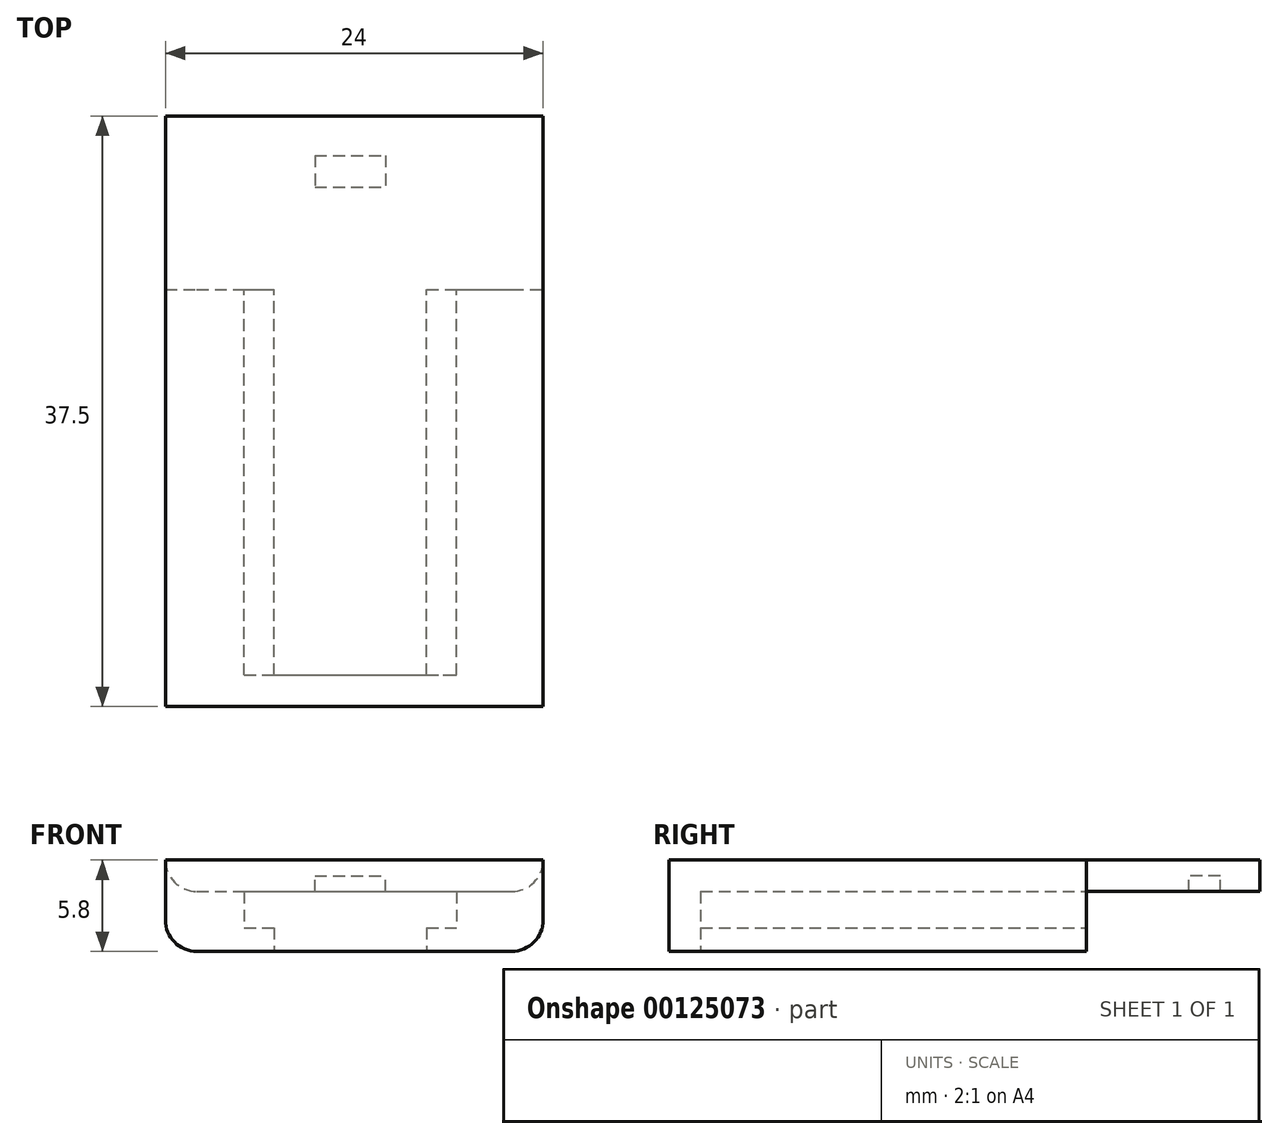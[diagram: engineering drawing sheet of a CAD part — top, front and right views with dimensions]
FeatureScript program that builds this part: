
annotation { "Feature Type Name" : "Feature", "Feature Type Description" : "" }
export const myFeature = defineFeature(function(context is Context, id is Id, definition is map)
    precondition{}
    {
        {
            var Q0;
            Q0=qCreatedBy(makeId("Front.planeOp"),FACE);
            var sketch = newSketch(context, id + "F0", { "sketchPlane" : qUnion([Q0])});
            skLineSegment(sketch, "E0.bottom", {"start": v(-6.75, 4.5) * mm, "end": v(-3.2, 4.5) * mm});
            skLineSegment(sketch, "E0.top", {"start": v(-6.75, 2.2) * mm, "end": v(-3.45, 2.2) * mm});
            skLineSegment(sketch, "E0.left", {"start": v(-6.75, 4.5) * mm, "end": v(-6.75, 2.2) * mm});
            skLineSegment(sketch, "E0.right", {"start": v(6.75, 4.5) * mm, "end": v(6.75, 2.2) * mm});
            skPoint(sketch, "E0.middle", {"position": v(0, 3.35) * mm});
            skLineSegment(sketch, "E1", {"start": v(4.85, 4.5) * mm, "end": v(4.85, 0) * mm});
            skLineSegment(sketch, "E2", {"start": v(-7.46, 0) * mm, "end": v(7.46, 0) * mm});
            skLineSegment(sketch, "E3.MirrorCS", {"start": v(-4.85, 4.5) * mm, "end": v(-4.85, 0) * mm});
            skLineSegment(sketch, "E4.trimOffspring", {"start": v(3.2, 4.5) * mm, "end": v(6.75, 4.5) * mm});
            skLineSegment(sketch, "E5.trimOffspring", {"start": v(3.45, 2.2) * mm, "end": v(6.75, 2.2) * mm});
            skLineSegment(sketch, "E6.top", {"start": v(-7.46, -2.58) * mm, "end": v(7.46, -2.58) * mm});
            skLineSegment(sketch, "E6.left", {"start": v(-7.46, 0) * mm, "end": v(-7.46, -2.58) * mm});
            skLineSegment(sketch, "E6.right", {"start": v(7.46, 0) * mm, "end": v(7.46, -2.58) * mm});
            skPoint(sketch, "E6.middle", {"position": v(0, -1.3) * mm});
            skLineSegment(sketch, "E7.bottom", {"start": v(-11.75, 6.5) * mm, "end": v(12.25, 6.5) * mm});
            skLineSegment(sketch, "E7.top", {"start": v(-11.75, 0.7) * mm, "end": v(-3.45, 0.7) * mm});
            skLineSegment(sketch, "E7.left", {"start": v(-11.75, 6.5) * mm, "end": v(-11.75, 0.7) * mm});
            skLineSegment(sketch, "E7.right", {"start": v(12.25, 6.5) * mm, "end": v(12.25, 0.7) * mm});
            skLineSegment(sketch, "E8.trimOffspring", {"start": v(3.45, 0.7) * mm, "end": v(12.25, 0.7) * mm});
            skLineSegment(sketch, "E9", {"start": v(-3.2, 4.5) * mm, "end": v(3.2, 4.5) * mm});
            skSolve(sketch);
        }
        {
            var Q0;
            {var subQ15=sQuery(id+"F0.wireOp",EDGE,"E0.left");Q0=makeQuery(id+"F0.imprint","IMPRINT",FACE,{"disambiguationData":[TD([[makeQuery(id+"F0.imprint","IMPRINT",EDGE,{"derivedFrom":subQ15}),-1.0]])]});}
            extrude(context, id + "F1", {"entities" : qUnion([Q0]), "depth" : 24.5 * mm});
        }
        {
            var Q0;
            Q0=makeQuery(id+"F1.opExtrude","CAP_FACE",FACE,{"disambiguationData":[OSD([sQuery(id+"F0.wireOp",EDGE,"E0.bottom"),sQuery(id+"F0.wireOp",EDGE,"E0.top"),sQuery(id+"F0.wireOp",EDGE,"E0.left"),sQuery(id+"F0.wireOp",EDGE,"E0.right"),sQuery(id+"F0.wireOp",EDGE,"S1AUJSAj-lBYP-Ti23-zWH8-DRC2IawmwYyc"),sQuery(id+"F0.wireOp",EDGE,"0b6ff6ab-89a0-4641-988e-e83ad78c142a0.MirrorCS"),sQuery(id+"F0.wireOp",EDGE,"E4.trimOffspring"),sQuery(id+"F0.wireOp",EDGE,"E5.trimOffspring"),sQuery(id+"F0.wireOp",EDGE,"E7.bottom"),sQuery(id+"F0.wireOp",EDGE,"E7.top"),sQuery(id+"F0.wireOp",EDGE,"E7.left"),sQuery(id+"F0.wireOp",EDGE,"E7.right"),sQuery(id+"F0.wireOp",EDGE,"E8.trimOffspring"),sQuery(id+"F0.wireOp",EDGE,"E9")])],"isStart":false});
            var sketch = newSketch(context, id + "F2", { "sketchPlane" : qUnion([Q0])});
            skLineSegment(sketch, "E10.bottom", {"start": v(-11.75, 6.5) * mm, "end": v(12.25, 6.5) * mm});
            skLineSegment(sketch, "E10.top", {"start": v(-11.75, 0.7) * mm, "end": v(12.25, 0.7) * mm});
            skLineSegment(sketch, "E10.left", {"start": v(-11.75, 6.5) * mm, "end": v(-11.75, 0.7) * mm});
            skLineSegment(sketch, "E10.right", {"start": v(12.25, 6.5) * mm, "end": v(12.25, 0.7) * mm});
            skSolve(sketch);
        }
        {
            var Q0;
            Q0 = qSketchRegion(id + "F2", true);
            extrude(context, id + "F3", {"entities" : qUnion([Q0]), "operationType" : NewBodyOperationType.ADD, "depth" : 2 * mm});
        }
        {
            var Q0;
            Q0=makeQuery(id+"F3.boolean.opBoolean","MERGE",FACE,{"derivedFrom":[makeQuery(id+"F1.opExtrude","SWEPT_FACE",FACE,{"disambiguationData":[OSD([sQuery(id+"F0.wireOp",EDGE,"E7.bottom")])]}),makeQuery(id+"F3.opExtrude","SWEPT_FACE",FACE,{"disambiguationData":[OSD([sQuery(id+"F2.wireOp",EDGE,"E10.bottom")])]})]});
            var sketch = newSketch(context, id + "F4", { "sketchPlane" : qUnion([Q0])});
            skLineSegment(sketch, "E11.bottom", {"start": v(-11.75, 0) * mm, "end": v(12.25, 0) * mm});
            skLineSegment(sketch, "E11.top", {"start": v(-11.75, 11) * mm, "end": v(12.25, 11) * mm});
            skLineSegment(sketch, "E11.left", {"start": v(-11.75, 0) * mm, "end": v(-11.75, 11) * mm});
            skLineSegment(sketch, "E11.right", {"start": v(12.25, 0) * mm, "end": v(12.25, 11) * mm});
            skLineSegment(sketch, "E12.bottom", {"start": v(-2.25, 8.5) * mm, "end": v(2.25, 8.5) * mm});
            skLineSegment(sketch, "E12.top", {"start": v(-2.25, 6.5) * mm, "end": v(2.25, 6.5) * mm});
            skLineSegment(sketch, "E12.left", {"start": v(-2.25, 8.5) * mm, "end": v(-2.25, 6.5) * mm});
            skLineSegment(sketch, "E12.right", {"start": v(2.25, 8.5) * mm, "end": v(2.25, 6.5) * mm});
            skPoint(sketch, "E12.middle", {"position": v(0, 7.5) * mm});
            skSolve(sketch);
        }
        {
            var Q0;
            Q0=makeQuery(id+"F4.imprint","IMPRINT",FACE,{"disambiguationData":[TD([[makeQuery(id+"F4.imprint","IMPRINT",EDGE,{"derivedFrom":sQuery(id+"F4.wireOp",EDGE,"E11.bottom")}),1.0]])]});
            extrude(context, id + "F5", {"entities" : qUnion([Q0]), "operationType" : NewBodyOperationType.ADD, "oppositeDirection" : true, "depth" : 2 * mm});
        }
        {
            var Q0;
            Q0=makeQuery(id+"F4.imprint","IMPRINT",FACE,{"disambiguationData":[TD([[makeQuery(id+"F4.imprint","IMPRINT",EDGE,{"derivedFrom":sQuery(id+"F4.wireOp",EDGE,"E12.bottom")}),-1.0]])]});
            extrude(context, id + "F6", {"entities" : qUnion([Q0]), "operationType" : NewBodyOperationType.ADD, "oppositeDirection" : true, "depth" : 1 * mm});
        }
        {
            var Q0;
            Q0=makeQuery(id+"F5.opExtrude","CAP_EDGE",EDGE,{"disambiguationData":[OSD([sQuery(id+"F4.wireOp",EDGE,"E11.left")])],"isStart":false});
            var Q1;
            Q1=makeQuery(id+"F5.opExtrude","CAP_EDGE",EDGE,{"disambiguationData":[OSD([sQuery(id+"F4.wireOp",EDGE,"E11.right")])],"isStart":false});
            var Q2;
            Q2=makeQuery(id+"F3.boolean.opBoolean","MERGE",EDGE,{"derivedFrom":[makeQuery(id+"F1.opExtrude","SWEPT_EDGE",EDGE,{"disambiguationData":[OSD([sQuery(id+"F0.wireOp",EDGE,"E7.top"),sQuery(id+"F0.wireOp",EDGE,"E7.left")])]}),makeQuery(id+"F3.opExtrude","SWEPT_EDGE",EDGE,{"disambiguationData":[OSD([sQuery(id+"F2.wireOp",EDGE,"E10.top"),sQuery(id+"F2.wireOp",EDGE,"E10.left")])]})]});
            var Q3;
            Q3=makeQuery(id+"F3.boolean.opBoolean","MERGE",EDGE,{"derivedFrom":[makeQuery(id+"F1.opExtrude","SWEPT_EDGE",EDGE,{"disambiguationData":[OSD([sQuery(id+"F0.wireOp",EDGE,"E7.right"),sQuery(id+"F0.wireOp",EDGE,"E8.trimOffspring")])]}),makeQuery(id+"F3.opExtrude","SWEPT_EDGE",EDGE,{"disambiguationData":[OSD([sQuery(id+"F2.wireOp",EDGE,"E10.top"),sQuery(id+"F2.wireOp",EDGE,"E10.right")])]})]});
            fillet(context, id + "F7", {"entities" : qUnion([Q0, Q1, Q2, Q3]), "radius" : 2 * mm, "tangentPropagation" : true, "allowEdgeOverflow" : false});
        }
    });
